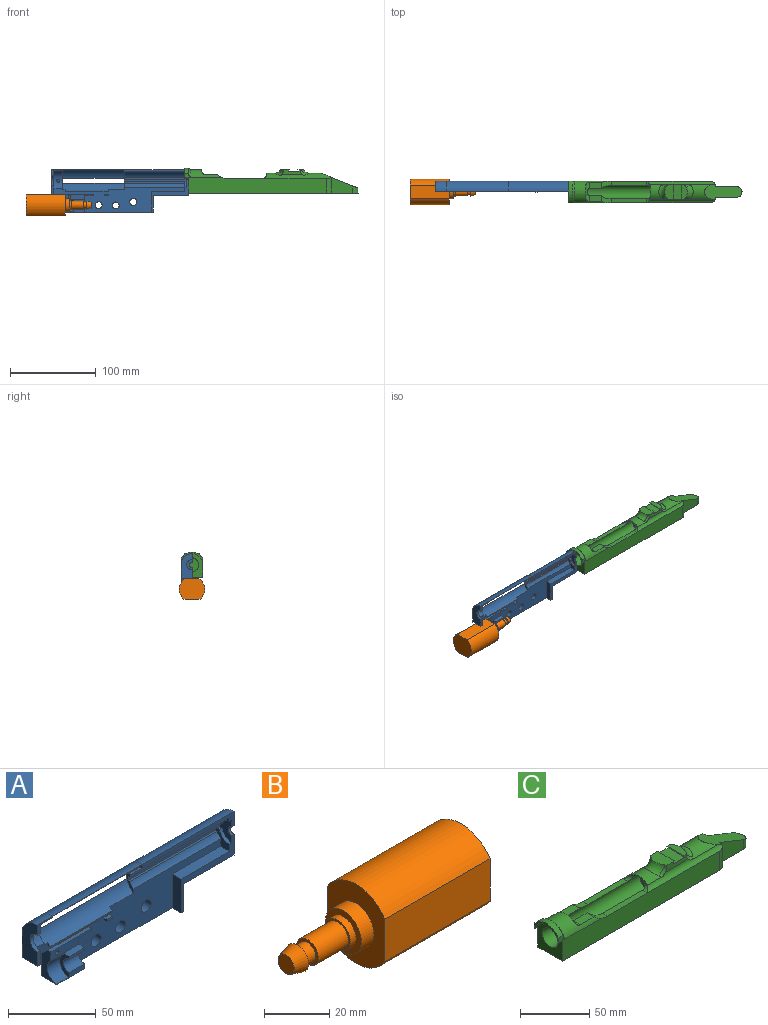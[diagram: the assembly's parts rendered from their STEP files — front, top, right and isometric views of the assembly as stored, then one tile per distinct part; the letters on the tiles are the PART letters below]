
ASSEMBLY  parts=3 mates=1
PART A: 67 faces, bbox 158.8x12.5x49.5 mm
  f0: plane 4.7x2.5mm, normal (0,0,1), area 11.8mm2, adj f2,f5,f61,f64
  f1: plane 4.7x2.5mm, normal (0,0,-1), area 11.8mm2, adj f2,f5,f61,f64
  f2: plane 4.7x1.5mm, normal (0,-1,0), area 7mm2, adj f0,f1,f61,f64
  f3: plane 19.1x7.2mm, normal (1,0,0), area 81.7mm2, adj f5,f8,f9,f11,f17,f26,f48,f60
  f4: plane 158.78x10mm, normal (0,-1,0), area 231.2mm2, adj f12,f15,f16,f19,f25,f36,f37,f38
  f5: plane 152.5x28.72mm, normal (0,-1,0), area 2209.7mm2, adj f0,f1,f3,f11,f13,f16,f20,f22
  f6: plane 158.78x40.07mm, normal (0,1,0), area 4647.1mm2, adj f7,f11,f12,f15,f22,f23,f24,f25
  f7: plane 20.6x12.5mm, normal (-1,0,0), area 139.1mm2, adj f6,f11,f13,f17,f26,f44,f48,f50
  f8: plane 12.5x1.9mm, normal (0,-1,0), area 23.8mm2, adj f3,f9,f48,f51
  f9: cylinder r=4.7mm len=12.5mm, axis (1,0,0), area 184.6mm2, adj f3,f8,f17,f51
  f10: plane 42.78x33.5mm, normal (0,-1,0), area 258.1mm2, adj f11,f12,f20,f21,f38,f40,f41,f45
  f11: plane 102.39x12.5mm, normal (0,0,-1), area 719.1mm2, adj f3,f5,f6,f7,f10,f17,f41,f46
  f12: plane 30.4x12.5mm, normal (1,0,0), area 334.9mm2, adj f4,f6,f10,f25,f38,f45
  f13: plane 32.8x2.5mm, normal (0,0,1), area 82mm2, adj f5,f7,f26,f63
  f14: plane 9.9x2.5mm, normal (0,-1,0), area 24.8mm2, adj f15,f16,f37,f44
  f15: plane 28.9x12.5mm, normal (-1,0,0), area 273.7mm2, adj f4,f6,f14,f25,f37,f44
  f16: plane 27.9x12mm, normal (1,0,0), area 203.2mm2, adj f4,f5,f14,f37,f44,f56
  f17: plane 22.5x3.3mm, normal (0,-1,0), area 44.2mm2, adj f3,f7,f9,f11,f50,f51
  f18: plane 50x0.89mm, normal (0,-1,0), area 44.3mm2, adj f27,f49,f54,f62
  f19: plane 11.3x9.7mm, normal (-1,0,0), area 37.1mm2, adj f4,f32,f33,f34,f35,f36,f39,f42
  f20: plane 12x11.3mm, normal (-1,0,0), area 60mm2, adj f5,f10,f21,f28,f29,f30,f31,f32
  f21: cylinder r=8mm len=7.84mm, axis (-1,0,0), area 21.9mm2, adj f10,f20,f40,f43
  f22: cylinder r=4.05mm len=8.1mm, axis (0,-1,0), area 134.9mm2, adj f5,f6
  f23: cylinder r=4.05mm len=8.1mm, axis (0,-1,0), area 134.9mm2, adj f5,f6
  f24: cylinder r=4.05mm len=8.1mm, axis (0,-1,0), area 134.9mm2, adj f5,f6
  f25: cylinder r=13mm len=158.78mm, axis (1,0,0), area 2668mm2, adj f4,f6,f12,f15
  f26: plane 32.8x6mm, normal (0,-1,0), area 142.9mm2, adj f3,f7,f13,f48,f60,f63,f65
  f27: plane 50x2.5mm, normal (0,0,-1), area 125mm2, adj f5,f18,f49,f62
  f28: cylinder r=10.6mm len=70.3mm, axis (1,0,0), area 348.4mm2, adj f5,f20,f29,f53
  f29: plane 70.3x1.37mm, normal (0,0,1), area 96.1mm2, adj f20,f28,f30,f53
  f30: plane 70.3x2.8mm, normal (0,-1,0), area 196.8mm2, adj f20,f29,f31,f53
  f31: plane 70.3x1.5mm, normal (0,0,-1), area 105.4mm2, adj f20,f30,f32,f53
  f32: plane 72.3x3.2mm, normal (0,-1,0), area 132.9mm2, adj f19,f20,f31,f33,f40,f42,f43,f53
  f33: plane 70.3x1.5mm, normal (0,0,1), area 105.4mm2, adj f19,f32,f34,f53
  f34: plane 70.3x2.8mm, normal (0,-1,0), area 196.8mm2, adj f19,f33,f35,f53
  f35: plane 70.3x1.37mm, normal (0,0,-1), area 96.1mm2, adj f19,f34,f36,f53
  f36: cylinder r=10.6mm len=70.3mm, axis (1,0,0), area 904.8mm2, adj f4,f19,f35,f53
  f37: cylinder r=6mm len=12mm, axis (1,0,0), area 47.1mm2, adj f4,f14,f15,f16
  f38: cylinder r=3mm len=6mm, axis (-1,0,0), area 16.8mm2, adj f4,f10,f12,f40
  f39: cylinder r=8mm len=7.84mm, axis (-1,0,0), area 21.9mm2, adj f4,f19,f40,f42
  f40: plane 16x9.8mm, normal (-1,0,0), area 92.3mm2, adj f4,f10,f21,f32,f38,f39,f42,f43
  f41: plane 23.6x7.2mm, normal (-1,0,0), area 169.9mm2, adj f5,f10,f11,f47
  f42: plane 2x1.96mm, normal (0,0,-1), area 3.9mm2, adj f19,f32,f39,f40
  f43: plane 2x1.96mm, normal (0,0,1), area 3.9mm2, adj f20,f21,f32,f40
  f44: plane 15.61x12.5mm, normal (0,0,-1), area 100.7mm2, adj f5,f6,f7,f14,f15,f16
  f45: plane 40.78x12.5mm, normal (0,0,-1), area 509.7mm2, adj f6,f10,f12,f46
  f46: plane 19.1x12.5mm, normal (1,0,0), area 238.8mm2, adj f6,f10,f11,f45
  f47: plane 39x7.2mm, normal (0,0,1), area 280.8mm2, adj f5,f10,f20,f41
  f48: plane 22.5x4.7mm, normal (0,0,1), area 66.1mm2, adj f3,f7,f8,f26,f50,f51
  f49: plane 2.5x2.2mm, normal (-1,0,0), area 3.7mm2, adj f5,f18,f27,f54
  f50: cylinder r=7.7mm len=14.3mm, axis (-1,0,0), area 200.2mm2, adj f7,f17,f48,f51
  f51: plane 14.3x7.7mm, normal (-1,0,0), area 55.5mm2, adj f8,f9,f17,f48,f50
  f52: plane 23.6x12.5mm, normal (1,0,0), area 26.6mm2, adj f4,f5,f6,f54,f55,f56
  f53: plane 23.6x12.5mm, normal (-1,0,0), area 61.2mm2, adj f4,f5,f6,f28,f29,f30,f31,f32
  f54: cylinder r=12.9mm len=72.2mm, axis (1,0,0), area 820.3mm2, adj f5,f6,f18,f49,f52,f53,f62
  f55: cylinder r=12.9mm len=72.2mm, axis (1,0,0), area 1230.5mm2, adj f4,f6,f52,f53
  f56: cylinder r=12mm len=21.6mm, axis (1,0,0), area 287.2mm2, adj f4,f5,f16,f52,f57
  f57: cylinder r=2mm len=4mm, axis (0,1,0), area 24.1mm2, adj f56,f59
  f58: plane 3x3mm, normal (0,-1,0), area 7.1mm2, adj f59
  f59: cone r=2mm half-angle=45deg, axis (0,1,0), area 7.8mm2, adj f57,f58
  f60: plane 10.3x2.5mm, normal (0,0,-1), area 25.8mm2, adj f3,f5,f26,f63
  f61: plane 2.5x1.5mm, normal (1,0,0), area 3.7mm2, adj f0,f1,f2,f5
  f62: plane 2.5x2.2mm, normal (1,0,0), area 3.7mm2, adj f5,f18,f27,f54
  f63: plane 2.5x1.5mm, normal (1,0,0), area 3.7mm2, adj f5,f13,f26,f60
  f64: plane 2.5x1.5mm, normal (-1,0,0), area 3.7mm2, adj f0,f1,f2,f5
  f65: cylinder r=1.55mm len=5mm, axis (0,-1,0), area 48.7mm2, adj f26,f66
  f66: plane 3.1x3.1mm, normal (0,-1,0), area 7.5mm2, adj f65
PART B: 16 faces, bbox 75.8x25x29.6 mm
  f0: cylinder r=14.8mm len=45.5mm, axis (1,0,0), area 1354.6mm2, adj f1,f2,f14,f15
  f1: plane 29.6x25mm, normal (1,0,0), area 638.7mm2, adj f0,f3,f14,f15
  f2: plane 29.6x25mm, normal (-1,0,0), area 450mm2, adj f0,f3,f4,f14,f15
  f3: cylinder r=14.8mm len=45.5mm, axis (1,0,0), area 1354.6mm2, adj f1,f2,f14,f15
  f4: cylinder r=7.75mm len=15.5mm, axis (1,0,0), area 267.8mm2, adj f2,f5
  f5: plane 15.5x15.5mm, normal (-1,0,0), area 93.7mm2, adj f4,f6
  f6: cylinder r=5.5mm len=11mm, axis (1,0,0), area 86.4mm2, adj f5,f7
  f7: plane 11x11mm, normal (-1,0,0), area 27.1mm2, adj f6,f8
  f8: cylinder r=4.65mm len=13mm, axis (1,0,0), area 379.8mm2, adj f7,f9
  f9: plane 9.3x9.3mm, normal (-1,0,0), area 29.4mm2, adj f8,f10
  f10: cylinder r=3.5mm len=7mm, axis (1,0,0), area 94.6mm2, adj f9,f11
  f11: plane 9.5x9.5mm, normal (1,0,0), area 32.4mm2, adj f10,f12
  f12: cone r=3.5mm half-angle=14deg, axis (1,0,0), area 133.6mm2, adj f11,f13
  f13: plane 7x7mm, normal (-1,0,0), area 38.5mm2, adj f12
  f14: plane 45.5x15.85mm, normal (0,1,0), area 721.1mm2, adj f0,f1,f2,f3
  f15: plane 45.5x15.85mm, normal (0,-1,0), area 721.1mm2, adj f0,f1,f2,f3
PART C: 52 faces, bbox 206.7x37.2x36.1 mm
  f0: plane 41x4.9mm, normal (0,0,1), area 200.9mm2, adj f4,f7,f11,f45
  f1: plane 41x4.9mm, normal (0,0,1), area 200.9mm2, adj f5,f6,f14,f45
  f2: plane 14x7.08mm, normal (0,0,1), area 99.1mm2, adj f5,f8,f19,f45
  f3: plane 14x7.08mm, normal (0,0,1), area 99.1mm2, adj f4,f8,f19,f45
  f4: cylinder r=18.25mm len=12mm, axis (0,-1,0), area 83.3mm2, adj f0,f3,f11,f19,f45
  f5: cylinder r=18.25mm len=12mm, axis (0,-1,0), area 83.3mm2, adj f1,f2,f14,f19,f45
  f6: cylinder r=4mm len=7.84mm, axis (0,1,0), area 22.1mm2, adj f1,f17,f18,f23,f45
  f7: cylinder r=4mm len=7.84mm, axis (0,1,0), area 22.1mm2, adj f0,f10,f18,f23,f45
  f8: cylinder r=4mm len=21.91mm, axis (0,-1,0), area 94.7mm2, adj f2,f3,f19,f22,f45
  f9: plane 17.5x6.5mm, normal (0,0,1), area 85.8mm2, adj f13,f24,f26,f27,f29,f44
  f10: cylinder r=5.12mm len=79.07mm, axis (1,0,0), area 419.7mm2, adj f7,f11,f16,f18,f26,f30,f31,f34
  f11: plane 165.54x22.96mm, normal (0,1,0), area 2805mm2, adj f0,f4,f10,f19,f20,f21,f41,f47
  f12: cylinder r=13.54mm len=0.91mm, axis (0,0,-1), area 0.4mm2, adj f15,f26,f31
  f13: cylinder r=13.54mm len=0.91mm, axis (0,0,-1), area 0.4mm2, adj f9,f27,f28
  f14: plane 165.54x22.96mm, normal (0,-1,0), area 2805mm2, adj f1,f5,f17,f19,f20,f21,f40,f47
  f15: plane 17.5x11mm, normal (0,0,1), area 162.3mm2, adj f12,f25,f26,f27,f32,f42
  f16: cylinder r=13.08mm len=26.28mm, axis (1,0,0), area 339.7mm2, adj f10,f17,f28,f29,f30,f34
  f17: cylinder r=5.12mm len=79.07mm, axis (1,0,0), area 419.7mm2, adj f6,f14,f16,f18,f27,f28,f33,f34
  f18: cylinder r=13.08mm len=17.81mm, axis (1,0,0), area 222.6mm2, adj f6,f7,f10,f17,f23,f31,f32,f33
  f19: cylinder r=13mm len=37.34mm, axis (-1,0,0), area 634.5mm2, adj f2,f3,f4,f5,f8,f11,f14,f22
  f20: plane 197.9x25mm, normal (0,0,-1), area 4514.9mm2, adj f11,f14,f21,f35,f36,f37,f38,f39
  f21: plane 27.5x25mm, normal (-1,0,0), area 424.5mm2, adj f11,f14,f20,f45,f47
  f22: plane 13.86x2mm, normal (1,0,0), area 18.8mm2, adj f8,f19
  f23: plane 15.38x2.5mm, normal (-1,0,0), area 16.7mm2, adj f6,f7,f18,f45
  f24: cylinder r=13.54mm len=0.91mm, axis (0,0,-1), area 0.4mm2, adj f9,f26,f30
  f25: cylinder r=13.54mm len=0.91mm, axis (0,0,-1), area 0.4mm2, adj f15,f27,f33
  f26: plane 23.82x6.21mm, normal (0,1,0), area 92.8mm2, adj f9,f10,f12,f15,f24,f30,f31,f42
  f27: plane 23.82x6.21mm, normal (0,-1,0), area 92.8mm2, adj f9,f13,f15,f17,f25,f28,f33,f42
  f28: bspline ~9.21x9.21mm, area 21mm2, adj f13,f16,f17,f27,f29
  f29: bspline ~17.34x10.24mm, area 136.9mm2, adj f9,f16,f28,f30
  f30: bspline ~9.42x9.41mm, area 21.1mm2, adj f10,f16,f24,f26,f29
  f31: bspline ~9.21x9.21mm, area 21mm2, adj f10,f12,f18,f26,f32
  f32: bspline ~17.34x10.24mm, area 136.9mm2, adj f15,f18,f31,f33
  f33: bspline ~9.42x9.41mm, area 21.1mm2, adj f17,f18,f25,f27,f32
  f34: plane 48.67x24.18mm, normal (0.37,0,0.93), area 580.8mm2, adj f10,f16,f17,f35,f36,f37,f38,f39
  f35: cylinder r=6mm len=12mm, axis (0,0,1), area 158.8mm2, adj f20,f34,f36,f39
  f36: plane 24.9x18.33mm, normal (0,-1,0), area 333.1mm2, adj f20,f34,f35,f37
  f37: plane 18.33x0.5mm, normal (1,0,0), area 9.2mm2, adj f20,f34,f36,f40
  f38: plane 18.33x0.5mm, normal (1,0,0), area 9.2mm2, adj f20,f34,f39,f41
  f39: plane 24.9x18.33mm, normal (0,1,0), area 333.1mm2, adj f20,f34,f35,f38
  f40: cylinder r=6mm len=18.7mm, axis (0,0,1), area 170.5mm2, adj f14,f17,f20,f34,f37
  f41: cylinder r=6mm len=18.7mm, axis (0,0,-1), area 170.5mm2, adj f10,f11,f20,f34,f38
  f42: plane 17x2mm, normal (0.87,0,-0.5), area 39.3mm2, adj f15,f26,f27,f43
  f43: plane 17x11.81mm, normal (0,0,1), area 200.8mm2, adj f26,f27,f42,f44
  f44: plane 17x2mm, normal (-0.87,0,-0.5), area 39.3mm2, adj f9,f26,f27,f43
  f45: cylinder r=8mm len=100mm, axis (-1,0,0), area 3862.6mm2, adj f0,f1,f2,f3,f4,f5,f6,f7
  f46: plane 16x16mm, normal (-1,0,0), area 201.1mm2, adj f45
  f47: cylinder r=13mm len=25mm, axis (1,0,0), area 134.4mm2, adj f11,f14,f21,f49
  f48: cylinder r=14.8mm len=25mm, axis (1,0,0), area 148.9mm2, adj f11,f14,f49,f50
  f49: plane 25x11.23mm, normal (-1,0,0), area 56.3mm2, adj f11,f14,f47,f48
  f50: plane 25x7.45mm, normal (1,0,0), area 9mm2, adj f11,f14,f48,f51
  f51: torus R=14.5mm, axis (-1,0,0), area 74.3mm2, adj f11,f14,f19,f50
PLACE A t=(-63.78,0,0)mm
PLACE B rot(axis=(0,-0.71,0.71),180deg) t=(-188.78,0,-28.5)mm
PLACE C at identity
MATE fastened A.f38 <-> C.f45  axis (1,0,0) through (0,0,0)mm
